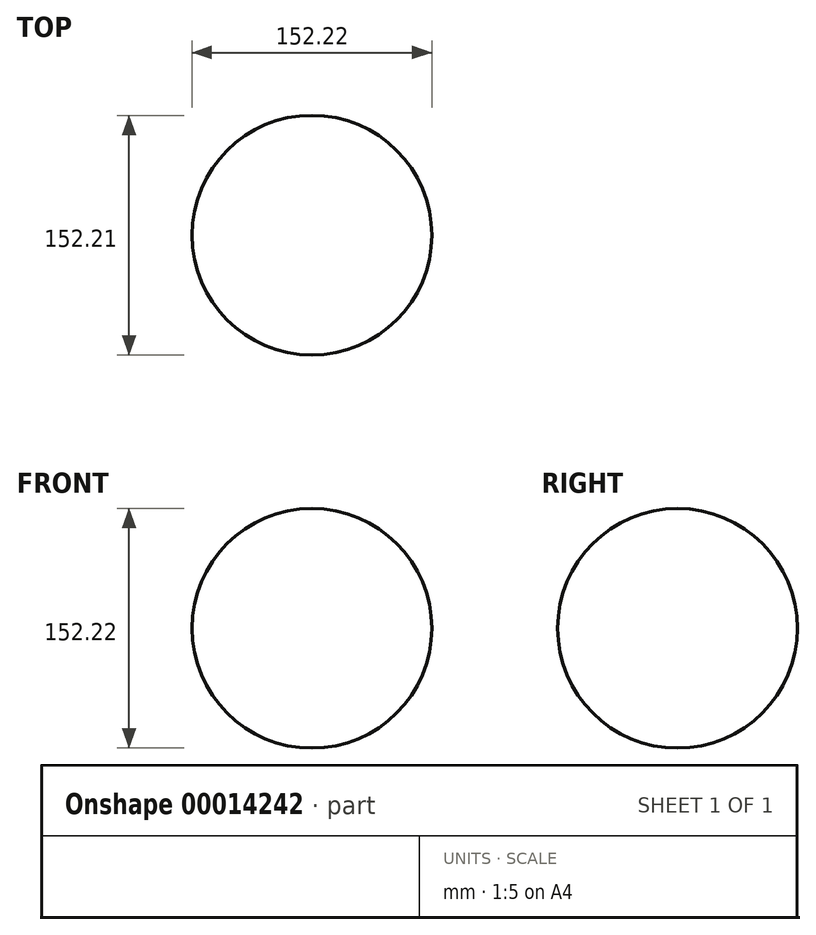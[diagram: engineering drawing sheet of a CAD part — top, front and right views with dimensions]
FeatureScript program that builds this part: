
annotation { "Feature Type Name" : "Feature", "Feature Type Description" : "" }
export const myFeature = defineFeature(function(context is Context, id is Id, definition is map)
    precondition{}
    {
        {
            var Q0;
            Q0=qCreatedBy(makeId("Top.planeOp"),FACE);
            var sketch = newSketch(context, id + "F0", { "sketchPlane" : qUnion([Q0])});
            skArc(sketch, "E0", {"start": v(0, -75.9) * mm, "mid": v(76.1, 0.2) * mm, "end": v(0, 76.31) * mm});
            skLineSegment(sketch, "E1", {"start": v(0, 76.31) * mm, "end": v(0, -75.9) * mm});
            skSolve(sketch);
        }
        {
            var Q0;
            Q0=makeQuery(id+"F0.imprint","IMPRINT",FACE,{"disambiguationData":[TD([[makeQuery(id+"F0.imprint","IMPRINT",EDGE,{"derivedFrom":sQuery(id+"F0.wireOp",EDGE,"E0")}),1.0]])]});
            var Q1;
            Q1=sQuery(id+"F0.wireOp",EDGE,"E1");
            revolve(context, id + "F1", {"entities" : qUnion([Q0]), "axis" : qUnion([Q1]), "revolveType" : RevolveType.FULL});
        }
    });
